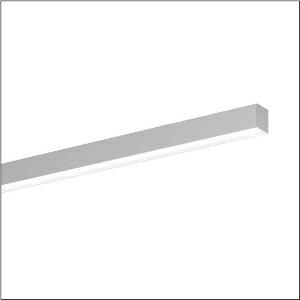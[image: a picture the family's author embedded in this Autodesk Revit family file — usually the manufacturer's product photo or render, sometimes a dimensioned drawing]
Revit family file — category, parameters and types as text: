
# Revit family: silica_21_51mx20da32sb
name_source: partatom
category: Lighting Fixtures
units: mm (PartAtom-declared; Revit-internal decimal feet)

## family parameters
Cut with Voids When Loaded = No
Host = Face
Light Source = No
Part Type = Normal
Room Calculation Point = No
Round Connector Dimension = Use Diameter
Shared = No

## types (1)
- --- (1 x LED, 2400 lm, 16.1 W, 3000K)
    Apparent Load = 16 VA
    CIE Flux Codes = 48 79 96 100 100
    Color Rendering = 80
    Color Temperature = 3000K
    Default Elevation = 1800 mm
    Description = Silica 21, office luminaire, primary optical cover: cover, of PMMA, opal, light emission: direct distribution, primary light characteristic: symmetric, installation type: surface-mounted, LED, rated luminous flux: 2.400lm, luminous efficacy: 149lm/W, light colour: 830, colour temperature: 3000K, control gear: DALI 2, with terminal, 3+2-pole, max. 2.5mm², mains connection: 220..240V, AC, 50/60Hz, rated input power: 16.1W, luminaire housing, of aluminium, metallic grey (RAL 9006), length: 1.204mm, width: 53mm, height: 53mm, protection rating (complete): IP20, insulation class (complete): insulation class I (protective earthing), certification: CE, permissible operating ambient temperature: 0..+35°C, standard: EN 50419, packaging unit: 1 piece
    Height = 53 mm
    Lamp = 1 x LED
    Lamp Light Flux = 2400 lm
    Lamp Power = 16.1 W
    Lamp count = 1
    Length = 1204 mm
    Luminous efficacy = 149 lm/W
    Manufacturer = Siteco
    ModVariant = No
    Model = 51MX20DA32SB
    Mounting Place = Ceiling
    Mounting Type = Surface mounted
    Number of Poles = 1
    OnlyDefault = Yes
    Power Factor = 1
    Product Name = Silica 21
    Product group = office luminaire | ceiling mounted
    ProductGroupID = 301
    Protection Class = Protection class I
    Protection Degree = IP 20
    RLX_Detail_Level = 1
    RLX_Emergency_Light_Flux = 0 lm
    RLX_Emergency_Type = 0
    RLX_Emergency_Type_DB = No
    RlxData = <blob elided: 26237 chars, md5=db14c495>
    Socket = socket
    Standby Power = 0 W
    System Light Flux = 2400 lm
    System Power = 16 W
    Type Comments = factory setting: luminous flux: 100 % | dim-lin: 254 | 233 mA
    Type Image = l_1335933.jpg
    URL = http://relux.com
    VarID = @adj_029315
    Voltage = 0 V
    Weight = 0.00 kg
    Width = 53 mm

## geometry (parser evidence)
native form markers: Blend x4, Sweep x11
no freeform markers — native parametric forms only
